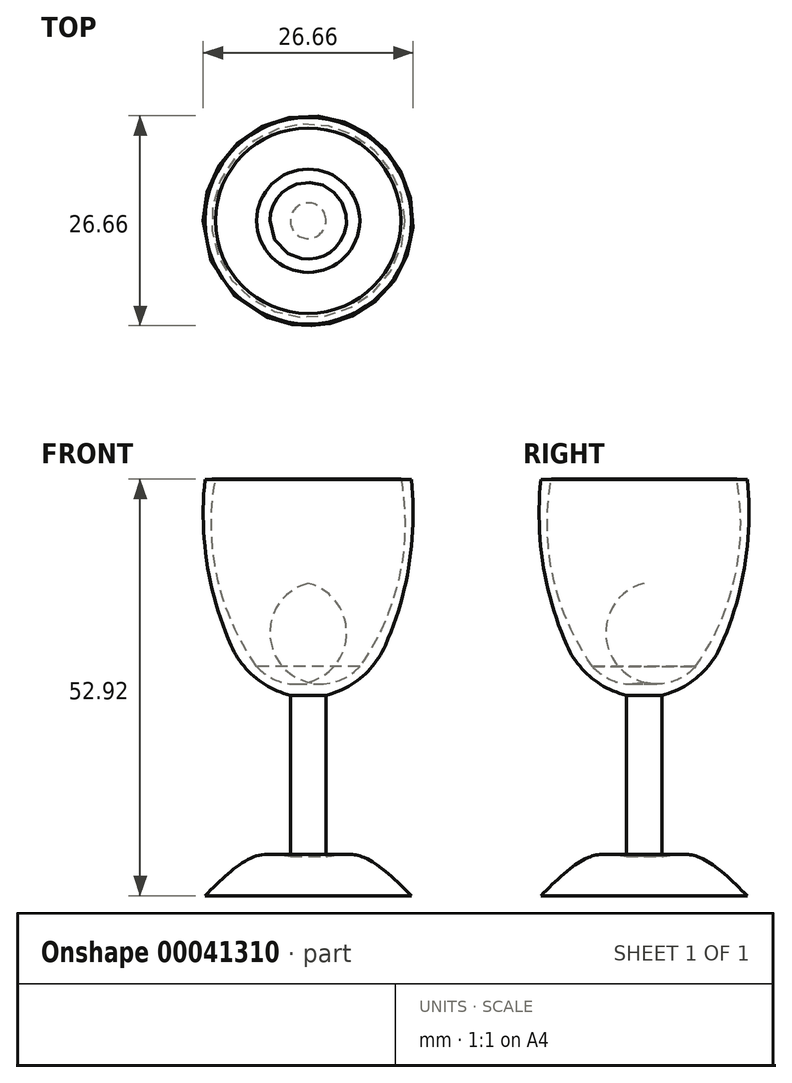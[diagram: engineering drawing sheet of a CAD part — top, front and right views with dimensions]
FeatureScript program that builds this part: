
annotation { "Feature Type Name" : "Feature", "Feature Type Description" : "" }
export const myFeature = defineFeature(function(context is Context, id is Id, definition is map)
    precondition{}
    {
        {
            var Q0;
            Q0=qCreatedBy(makeId("Right.planeOp"),FACE);
            var sketch = newSketch(context, id + "F0", { "sketchPlane" : qUnion([Q0])});
            skArc(sketch, "E0", {"start": v(9.8, 31.8) * mm, "mid": v(12.83, 42.12) * mm, "end": v(13.1, 52.89) * mm});
            skLineSegment(sketch, "E1", {"start": v(2.26, 25.46) * mm, "end": v(2.26, 4.97) * mm});
            skArc(sketch, "E2", {"start": v(9.8, 31.8) * mm, "mid": v(6.76, 27.75) * mm, "end": v(2.26, 25.46) * mm});
            skFitSpline(sketch, "E3", {"points": [v(2.26, 4.97) * mm, v(6.78, 4.97) * mm, v(13.1, 0) * mm], "startDerivative": vector(10.44, 1.86) * mm, "endDerivative": vector(11.22, -11.19) * mm});
            skLineSegment(sketch, "E4", {"start": v(0, 0) * mm, "end": v(13.1, 0) * mm});
            skLineSegment(sketch, "E5", {"start": v(0, 53.19) * mm, "end": v(0, 0) * mm});
            skLineSegment(sketch, "E6", {"start": v(0, 53.19) * mm, "end": v(0, 68.26) * mm, "construction": true});
            skLineSegment(sketch, "E7", {"start": v(0, 53.19) * mm, "end": v(13.1, 52.89) * mm});
            skSolve(sketch);
        }
        {
            var Q0;
            Q0=qCreatedBy(makeId("Right.planeOp"),FACE);
            var sketch = newSketch(context, id + "F1", { "sketchPlane" : qUnion([Q0])});
            skLineSegment(sketch, "E8", {"start": v(0, 53.8) * mm, "end": v(11.6, 53.8) * mm});
            skArc(sketch, "E9", {"start": v(6.56, 29.15) * mm, "mid": v(11.65, 40.94) * mm, "end": v(11.6, 53.8) * mm});
            skArc(sketch, "E10", {"start": v(0, 27.1) * mm, "mid": v(3.57, 27.19) * mm, "end": v(6.56, 29.15) * mm});
            skLineSegment(sketch, "E11", {"start": v(0, 53.8) * mm, "end": v(0, 60.39) * mm, "construction": true});
            skLineSegment(sketch, "E12", {"start": v(0, 53.8) * mm, "end": v(0, 27.1) * mm});
            skSolve(sketch);
        }
        {
            var Q0;
            Q0 = qSketchRegion(id + "F0", true);
            var Q1;
            Q1=sQuery(id+"F0.wireOp",EDGE,"E6");
            revolve(context, id + "F2", {"entities" : qUnion([Q0]), "axis" : qUnion([Q1]), "revolveType" : RevolveType.FULL});
        }
        {
            var Q0;
            Q0 = qSketchRegion(id + "F1", true);
            var Q1;
            Q1 = qConstructionFilter(qBodyType(qCreatedBy(id + "F1" ,EDGE), BodyType.WIRE), ConstructionObject.NO);
            var Q2;
            Q2=sQuery(id+"F1.wireOp",EDGE,"E11");
            revolve(context, id + "F3", {"operationType" : NewBodyOperationType.REMOVE, "entities" : qUnion([Q0]), "surfaceEntities" : qUnion([Q1]), "axis" : qUnion([Q2]), "revolveType" : RevolveType.FULL, "oppositeDirection" : true});
        }
    });
